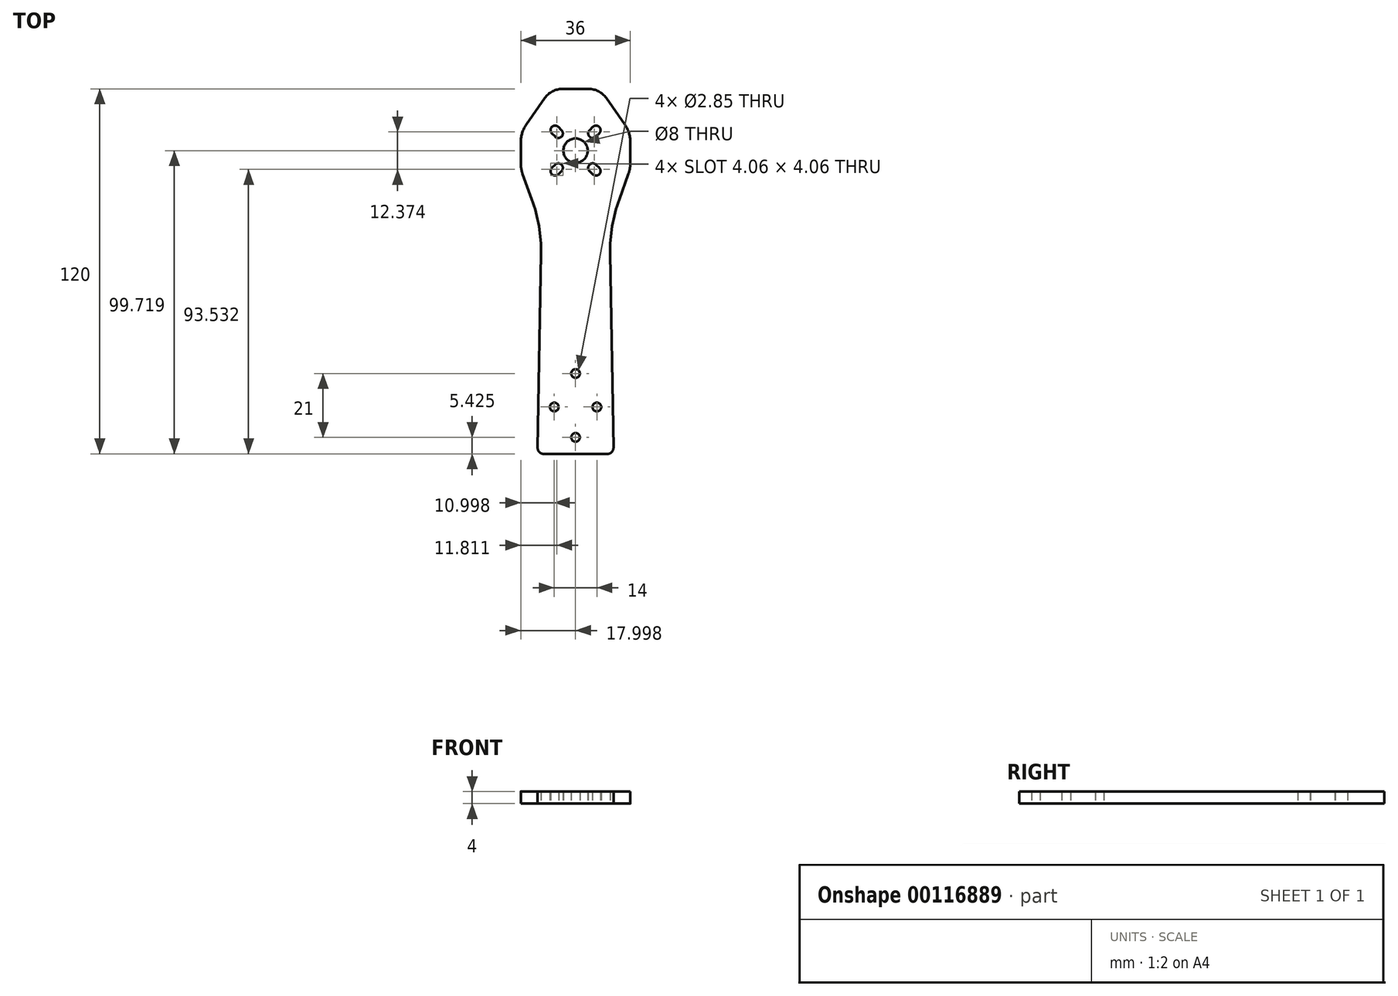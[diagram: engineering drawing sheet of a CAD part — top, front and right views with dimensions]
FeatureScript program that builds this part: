
annotation { "Feature Type Name" : "Feature", "Feature Type Description" : "" }
export const myFeature = defineFeature(function(context is Context, id is Id, definition is map)
    precondition{}
    {
        {
            var Q0;
            Q0=qCreatedBy(makeId("Top.planeOp"),FACE);
            var sketch = newSketch(context, id + "F0", { "sketchPlane" : qUnion([Q0])});
            skLineSegment(sketch, "E0", {"start": v(-48.38, 56.52) * mm, "end": v(-39.67, 56.52) * mm});
            skLineSegment(sketch, "E1", {"start": v(-33.93, 53.54) * mm, "end": v(-27.83, 44.82) * mm});
            skLineSegment(sketch, "E2", {"start": v(-26.02, 39.09) * mm, "end": v(-26.02, 32) * mm});
            skLineSegment(sketch, "E3", {"start": v(-26.63, 28.58) * mm, "end": v(-32.83, 11.53) * mm});
            skLineSegment(sketch, "E4", {"start": v(-32.83, 11.53) * mm, "end": v(-31.56, -61.44) * mm});
            skLineSegment(sketch, "E5", {"start": v(-33.56, -63.48) * mm, "end": v(-54.49, -63.48) * mm});
            skLineSegment(sketch, "E6", {"start": v(-56.49, -61.44) * mm, "end": v(-55.21, 11.53) * mm});
            skLineSegment(sketch, "E7", {"start": v(-55.21, 11.53) * mm, "end": v(-61.42, 28.58) * mm});
            skLineSegment(sketch, "E8", {"start": v(-62.02, 32) * mm, "end": v(-62.02, 39.09) * mm});
            skLineSegment(sketch, "E9", {"start": v(-60.21, 44.82) * mm, "end": v(-54.11, 53.54) * mm});
            skPoint(sketch, "E10", {"position": v(-44.02, 56.52) * mm});
            skPoint(sketch, "E11", {"position": v(-44.02, -63.48) * mm});
            skPoint(sketch, "E12.centerSnap0", {"position": v(-62.02, 36.24) * mm});
            skCircle(sketch, "E13", {"center": v(-51.02, -58.05) * mm, "radius": 1.43 * mm});
            skCircle(sketch, "E14", {"center": v(-51.02, -48.05) * mm, "radius": 1.43 * mm});
            skCircle(sketch, "E15", {"center": v(-37.02, -48.05) * mm, "radius": 1.43 * mm});
            skCircle(sketch, "E16", {"center": v(-37.02, -58.05) * mm, "radius": 1.43 * mm});
            skPoint(sketch, "E17.visualSharp", {"position": v(-52.02, 56.52) * mm});
            skArc(sketch, "E17.filletArc", {"start": v(-48.38, 56.52) * mm, "mid": v(-51.61, 55.73) * mm, "end": v(-54.11, 53.54) * mm});
            skPoint(sketch, "E18.visualSharp", {"position": v(-36.02, 56.52) * mm});
            skArc(sketch, "E18.filletArc", {"start": v(-33.93, 53.54) * mm, "mid": v(-36.43, 55.73) * mm, "end": v(-39.67, 56.52) * mm});
            skPoint(sketch, "E19.visualSharp", {"position": v(-26.02, 42.24) * mm});
            skArc(sketch, "E19.filletArc", {"start": v(-26.02, 39.09) * mm, "mid": v(-26.48, 42.1) * mm, "end": v(-27.83, 44.82) * mm});
            skPoint(sketch, "E20.visualSharp", {"position": v(-62.02, 42.24) * mm});
            skArc(sketch, "E20.filletArc", {"start": v(-60.21, 44.82) * mm, "mid": v(-61.56, 42.1) * mm, "end": v(-62.02, 39.09) * mm});
            skPoint(sketch, "E21.visualSharp", {"position": v(-62.02, 30.24) * mm});
            skArc(sketch, "E21.filletArc", {"start": v(-62.02, 32) * mm, "mid": v(-61.87, 30.27) * mm, "end": v(-61.42, 28.58) * mm});
            skPoint(sketch, "E22.visualSharp", {"position": v(-26.02, 30.24) * mm});
            skArc(sketch, "E22.filletArc", {"start": v(-26.63, 28.58) * mm, "mid": v(-26.17, 30.27) * mm, "end": v(-26.02, 32) * mm});
            skCircle(sketch, "E23", {"center": v(-105.37, 3.14) * mm, "radius": 50 * mm});
            skCircle(sketch, "E24", {"center": v(17.32, 3.14) * mm, "radius": 50 * mm});
            skPoint(sketch, "E25.visualSharp", {"position": v(-56.52, -63.48) * mm});
            skArc(sketch, "E25.filletArc", {"start": v(-56.49, -61.44) * mm, "mid": v(-55.91, -62.88) * mm, "end": v(-54.49, -63.48) * mm});
            skPoint(sketch, "E26.visualSharp", {"position": v(-31.52, -63.48) * mm});
            skArc(sketch, "E26.filletArc", {"start": v(-33.56, -63.48) * mm, "mid": v(-32.13, -62.88) * mm, "end": v(-31.56, -61.44) * mm});
            skCircle(sketch, "E27", {"center": v(-44.02, 36.24) * mm, "radius": 80 * mm});
            skCircle(sketch, "E28", {"center": v(-44.02, 36.24) * mm, "radius": 4 * mm});
            skLineSegment(sketch, "E29", {"start": v(-62.02, 36.24) * mm, "end": v(-26.02, 36.24) * mm});
            skLineSegment(sketch, "E30", {"start": v(-51.8, 30.58) * mm, "end": v(-50.74, 31.64) * mm});
            skLineSegment(sketch, "E31", {"start": v(-48.62, 31.64) * mm, "end": v(-48.62, 31.64) * mm});
            skLineSegment(sketch, "E32", {"start": v(-48.62, 29.52) * mm, "end": v(-49.68, 28.46) * mm});
            skLineSegment(sketch, "E33", {"start": v(-51.8, 28.46) * mm, "end": v(-51.8, 28.46) * mm});
            skLineSegment(sketch, "E34", {"start": v(-39.43, 29.52) * mm, "end": v(-38.37, 28.46) * mm});
            skLineSegment(sketch, "E35", {"start": v(-36.24, 28.46) * mm, "end": v(-36.24, 28.46) * mm});
            skLineSegment(sketch, "E36", {"start": v(-36.24, 30.58) * mm, "end": v(-37.3, 31.64) * mm});
            skLineSegment(sketch, "E37", {"start": v(-39.43, 31.64) * mm, "end": v(-39.43, 31.64) * mm});
            skLineSegment(sketch, "E38", {"start": v(-48.62, 31.64) * mm, "end": v(-42.36, 37.9) * mm});
            skLineSegment(sketch, "E39", {"start": v(-39.43, 31.64) * mm, "end": v(-43.24, 35.45) * mm});
            skPoint(sketch, "E40.visualSharp", {"position": v(-49.68, 32.7) * mm});
            skArc(sketch, "E40.filletArc", {"start": v(-48.62, 31.64) * mm, "mid": v(-49.68, 32.08) * mm, "end": v(-50.74, 31.64) * mm});
            skPoint(sketch, "E41.visualSharp", {"position": v(-47.56, 30.58) * mm});
            skArc(sketch, "E41.filletArc", {"start": v(-48.62, 29.52) * mm, "mid": v(-48.18, 30.58) * mm, "end": v(-48.62, 31.64) * mm});
            skPoint(sketch, "E42.visualSharp", {"position": v(-52.86, 29.52) * mm});
            skArc(sketch, "E42.filletArc", {"start": v(-51.8, 30.58) * mm, "mid": v(-52.24, 29.52) * mm, "end": v(-51.8, 28.46) * mm});
            skPoint(sketch, "E43.visualSharp", {"position": v(-50.74, 27.4) * mm});
            skArc(sketch, "E43.filletArc", {"start": v(-51.8, 28.46) * mm, "mid": v(-50.74, 28.02) * mm, "end": v(-49.68, 28.46) * mm});
            skPoint(sketch, "E44.visualSharp", {"position": v(-40.49, 30.58) * mm});
            skArc(sketch, "E44.filletArc", {"start": v(-39.43, 31.64) * mm, "mid": v(-39.87, 30.58) * mm, "end": v(-39.43, 29.52) * mm});
            skPoint(sketch, "E45.visualSharp", {"position": v(-38.37, 32.7) * mm});
            skArc(sketch, "E45.filletArc", {"start": v(-37.3, 31.64) * mm, "mid": v(-38.37, 32.08) * mm, "end": v(-39.43, 31.64) * mm});
            skPoint(sketch, "E46.visualSharp", {"position": v(-35.18, 29.52) * mm});
            skArc(sketch, "E46.filletArc", {"start": v(-36.24, 28.46) * mm, "mid": v(-35.8, 29.52) * mm, "end": v(-36.24, 30.58) * mm});
            skPoint(sketch, "E47.visualSharp", {"position": v(-37.3, 27.4) * mm});
            skArc(sketch, "E47.filletArc", {"start": v(-38.37, 28.46) * mm, "mid": v(-37.3, 28.02) * mm, "end": v(-36.24, 28.46) * mm});
            skArc(sketch, "E48.MirrorCS", {"start": v(-48.62, 42.96) * mm, "mid": v(-48.18, 41.9) * mm, "end": v(-48.62, 40.84) * mm});
            skPoint(sketch, "E49.MirrorP", {"position": v(-50.74, 45.08) * mm});
            skArc(sketch, "E50.MirrorCS", {"start": v(-51.8, 44.02) * mm, "mid": v(-50.74, 44.46) * mm, "end": v(-49.68, 44.02) * mm});
            skLineSegment(sketch, "E51.MirrorCS", {"start": v(-51.8, 44.02) * mm, "end": v(-51.8, 44.02) * mm});
            skLineSegment(sketch, "E52.MirrorCS", {"start": v(-48.62, 42.96) * mm, "end": v(-49.68, 44.02) * mm});
            skArc(sketch, "E53.MirrorCS", {"start": v(-51.8, 41.9) * mm, "mid": v(-52.24, 42.96) * mm, "end": v(-51.8, 44.02) * mm});
            skLineSegment(sketch, "E54.MirrorCS", {"start": v(-51.8, 41.9) * mm, "end": v(-50.74, 40.84) * mm});
            skPoint(sketch, "E55.MirrorP", {"position": v(-52.86, 42.96) * mm});
            skPoint(sketch, "E56.MirrorP", {"position": v(-47.56, 41.9) * mm});
            skArc(sketch, "E57.MirrorCS", {"start": v(-48.62, 40.84) * mm, "mid": v(-49.68, 40.4) * mm, "end": v(-50.74, 40.84) * mm});
            skLineSegment(sketch, "E58.MirrorCS", {"start": v(-36.24, 41.9) * mm, "end": v(-37.3, 40.84) * mm});
            skLineSegment(sketch, "E59.MirrorCS", {"start": v(-36.24, 44.02) * mm, "end": v(-36.24, 44.02) * mm});
            skPoint(sketch, "E60.MirrorP", {"position": v(-35.18, 42.96) * mm});
            skPoint(sketch, "E61.MirrorP", {"position": v(-40.49, 41.9) * mm});
            skArc(sketch, "E62.MirrorCS", {"start": v(-38.37, 44.02) * mm, "mid": v(-37.3, 44.46) * mm, "end": v(-36.24, 44.02) * mm});
            skLineSegment(sketch, "E63.MirrorCS", {"start": v(-39.43, 42.96) * mm, "end": v(-38.37, 44.02) * mm});
            skArc(sketch, "E64.MirrorCS", {"start": v(-39.43, 40.84) * mm, "mid": v(-39.87, 41.9) * mm, "end": v(-39.43, 42.96) * mm});
            skArc(sketch, "E65.MirrorCS", {"start": v(-36.24, 44.02) * mm, "mid": v(-35.8, 42.96) * mm, "end": v(-36.24, 41.9) * mm});
            skPoint(sketch, "E66.MirrorP", {"position": v(-37.3, 45.08) * mm});
            skArc(sketch, "E67.MirrorCS", {"start": v(-37.3, 40.84) * mm, "mid": v(-38.37, 40.4) * mm, "end": v(-39.43, 40.84) * mm});
            skCircle(sketch, "E68", {"center": v(-44.02, -37.05) * mm, "radius": 1.43 * mm});
            skCircle(sketch, "E69", {"center": v(-44.02, -58.05) * mm, "radius": 1.43 * mm});
            skSolve(sketch);
        }
        {
            var Q0;
            {var subQ0=sQuery(id+"F0.wireOp",EDGE,"E4");var subQ1=sQuery(id+"F0.wireOp",EDGE,"E3");var subQ2=makeQuery(id+"F0.imprint","INTERSECT",VERTEX,{"derivedFrom":[subQ1,subQ0]});Q0=makeQuery(id+"F0.imprint","IMPRINT",FACE,{"disambiguationData":[TD([[makeQuery(id+"F0.imprint","IMPRINT",EDGE,{"disambiguationData":[TD([[subQ2,1.0]])],"derivedFrom":subQ1}),1.0]])]});}
            var Q1;
            {var subQ0=sQuery(id+"F0.wireOp",EDGE,"E7");var subQ1=sQuery(id+"F0.wireOp",EDGE,"E6");var subQ2=makeQuery(id+"F0.imprint","INTERSECT",VERTEX,{"derivedFrom":[subQ1,subQ0]});Q1=makeQuery(id+"F0.imprint","IMPRINT",FACE,{"disambiguationData":[TD([[makeQuery(id+"F0.imprint","IMPRINT",EDGE,{"disambiguationData":[TD([[subQ2,1.0]])],"derivedFrom":subQ1}),1.0]])]});}
            var Q2;
            Q2=makeQuery(id+"F0.imprint","IMPRINT",FACE,{"disambiguationData":[TD([[makeQuery(id+"F0.imprint","IMPRINT",EDGE,{"derivedFrom":sQuery(id+"F0.wireOp",EDGE,"E0")}),-1.0]])]});
            var Q3;
            Q3=makeQuery(id+"F0.imprint","IMPRINT",FACE,{"disambiguationData":[TD([[makeQuery(id+"F0.imprint","IMPRINT",EDGE,{"derivedFrom":sQuery(id+"F0.wireOp",EDGE,"E12")}),1.0]])]});
            var Q4;
            Q4=makeQuery(id+"F0.imprint","IMPRINT",FACE,{"disambiguationData":[TD([[makeQuery(id+"F0.imprint","IMPRINT",EDGE,{"derivedFrom":sQuery(id+"F0.wireOp",EDGE,"E5")}),-1.0]])]});
            var Q5;
            {var subQ11=sQuery(id+"F0.wireOp",EDGE,"E21.filletArc");Q5=makeQuery(id+"F0.imprint","IMPRINT",FACE,{"disambiguationData":[TD([[makeQuery(id+"F0.imprint","IMPRINT",EDGE,{"derivedFrom":subQ11}),1.0]])]});}
            var Q6;
            Q6=makeQuery(id+"F0.imprint","IMPRINT",FACE,{"disambiguationData":[TD([[makeQuery(id+"F0.imprint","IMPRINT",EDGE,{"derivedFrom":sQuery(id+"F0.wireOp",EDGE,"E13")}),1.0]])]});
            var Q7;
            Q7=makeQuery(id+"F0.imprint","IMPRINT",FACE,{"disambiguationData":[TD([[makeQuery(id+"F0.imprint","IMPRINT",EDGE,{"derivedFrom":sQuery(id+"F0.wireOp",EDGE,"E16")}),1.0]])]});
            extrude(context, id + "F1", {"entities" : qUnion([Q0, Q1, Q2, Q3, Q4, Q5, Q6, Q7]), "depth" : 4 * mm});
        }
    });
